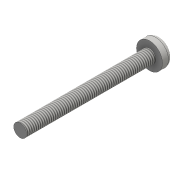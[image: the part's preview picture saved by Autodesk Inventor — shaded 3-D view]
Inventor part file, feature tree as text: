
AUTODESK INVENTOR PART (.ipt)
format: ipt  version: 2016 (Build 200138000, 138)  size: 109,568 bytes
history: native  units: mm
features: extrude x3, sketch x3, fillet x1, thread x1
ambient origin geometry x8: Origin, YZ Plane, XZ Plane, XY Plane, X Axis, Y Axis, Z Axis, Center Point
bodies: Solid1 (feature_tree)
feature tree (8):
  extrude  "Extrusion1"  Depth=2.4mm TaperAngle=0.0deg
  extrude  "Extrusion2"  Depth=0.5mm
  fillet  "Fillet1"  Radius=0.5mm
  extrude  "Extrusion3"  Depth=1.0mm TaperAngle=0.0deg
  thread  "Thread1"  [1 undecoded]
  sketch  "Sketch1"  dims[d0=6.0mm d1=2.4mm d2=0.0mm]
  sketch  "Sketch2"  dims[d5=3.1mm d6=0.5mm d9=0.5mm]
  sketch  "Sketch3"  dims[d10=3.1mm d11=1.0mm d12=0.0mm d13=1.0mm d14=3.0mm d15=30.0mm d16=0.0mm d17=10.0mm d18=0.0mm]
note: 1 required parameter value undecoded (feature->parameter linkage not recoverable at this tier; creation-order binding heuristic only, values carry confidence <= 0.55)
